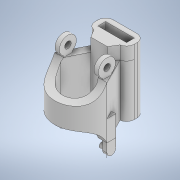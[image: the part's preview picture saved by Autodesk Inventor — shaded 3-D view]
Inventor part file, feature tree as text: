
AUTODESK INVENTOR PART (.ipt)
format: ipt  version: 2022 (Build 260153000, 153)  size: 323,584 bytes
history: native  units: mm
features: extrude x16, sketch x10, other x2, shell x1, fillet x1, projected_geometry x1
ambient origin geometry x8: Origin, YZ Plane, XZ Plane, XY Plane, X Axis, Y Axis, Z Axis, Center Point
bodies: Body1 (feature_tree)
feature tree (31):
  other  "솔리드1"
  extrude  "돌출1"  Depth=20.0mm
  sketch  "스케치2"
  shell  "쉘1"  Thickness=10.0mm
  extrude  "돌출3"  Depth=5.0mm
  sketch  "스케치8"
  extrude  "돌출7"  Depth=20.0mm TaperAngle=0.0deg
  sketch  "스케치9"
  extrude  "돌출8"  Depth=6.0mm
  extrude  "돌출9"  Depth=3.0mm
  sketch  "스케치11"
  extrude  "돌출10"  Depth=30.0mm TaperAngle=0.0deg
  sketch  "스케치12"
  extrude  "돌출11"  Depth=30.0mm TaperAngle=0.0deg
  extrude  "돌출12"  Depth=5.0mm TaperAngle=0.0deg
  extrude  "돌출13"  Depth=5.0mm TaperAngle=0.0deg
  sketch  "스케치14"
  extrude  "돌출15"  Depth=6.5mm
  other  "작업 평면1"
  extrude  "돌출16"  Depth=2.5mm
  fillet  "모깎기1"  Radius=8.0mm
  extrude  "돌출17"  Depth=2.0mm
  extrude  "돌출18"  Depth=100.0mm TaperAngle=0.0deg
  extrude  "돌출19"  Depth=2.0mm TaperAngle=0.0deg
  extrude  "돌출20"  Depth=2.0mm TaperAngle=0.0deg
  extrude  "돌출21"  Depth=5.0mm TaperAngle=0.0deg
  sketch  "스케치1"
  sketch  "스케치13"
  projected_geometry  "투영된 루프1"
  sketch  "스케치15"
  sketch  "스케치16"
